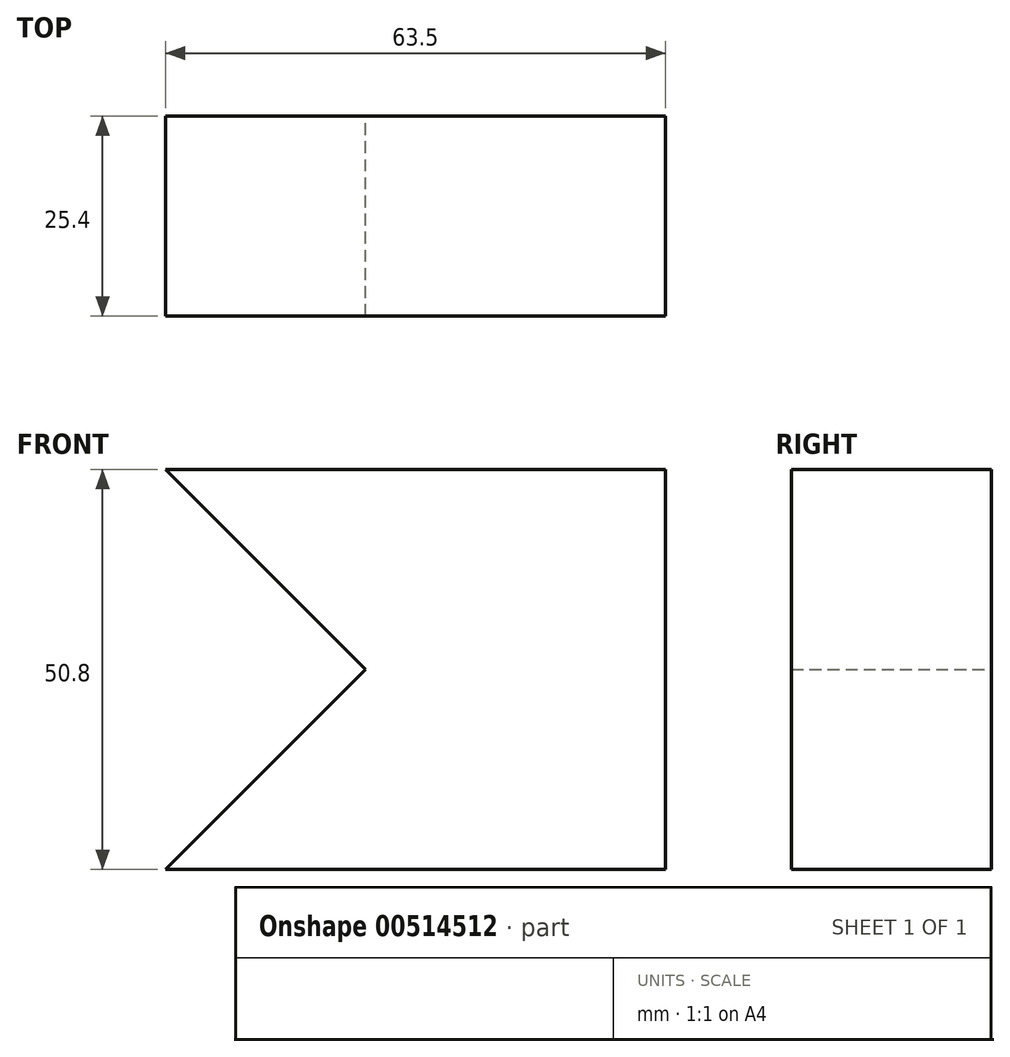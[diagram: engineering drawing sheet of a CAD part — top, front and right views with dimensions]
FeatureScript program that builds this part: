
annotation { "Feature Type Name" : "Feature", "Feature Type Description" : "" }
export const myFeature = defineFeature(function(context is Context, id is Id, definition is map)
    precondition{}
    {
        {
            var Q0;
            Q0=qCreatedBy(makeId("Front.planeOp"),FACE);
            var sketch = newSketch(context, id + "F0", { "sketchPlane" : qUnion([Q0])});
            skLineSegment(sketch, "E0", {"start": v(0, 0) * mm, "end": v(-25.4, 25.4) * mm});
            skLineSegment(sketch, "E1", {"start": v(-25.4, 25.4) * mm, "end": v(38.1, 25.4) * mm});
            skLineSegment(sketch, "E2", {"start": v(38.1, 25.4) * mm, "end": v(38.1, -25.4) * mm});
            skLineSegment(sketch, "E3", {"start": v(38.1, -25.4) * mm, "end": v(-25.4, -25.4) * mm});
            skLineSegment(sketch, "E4", {"start": v(-25.4, -25.4) * mm, "end": v(0, 0) * mm});
            skSolve(sketch);
        }
        {
            var Q0;
            Q0=makeQuery(id+"F0.imprint","IMPRINT",FACE,{"disambiguationData":[TD([[makeQuery(id+"F0.imprint","IMPRINT",EDGE,{"derivedFrom":sQuery(id+"F0.wireOp",EDGE,"E0")}),-1.0]])]});
            extrude(context, id + "F1", {"entities" : qUnion([Q0]), "depth" : 25.4 * mm});
        }
    });
